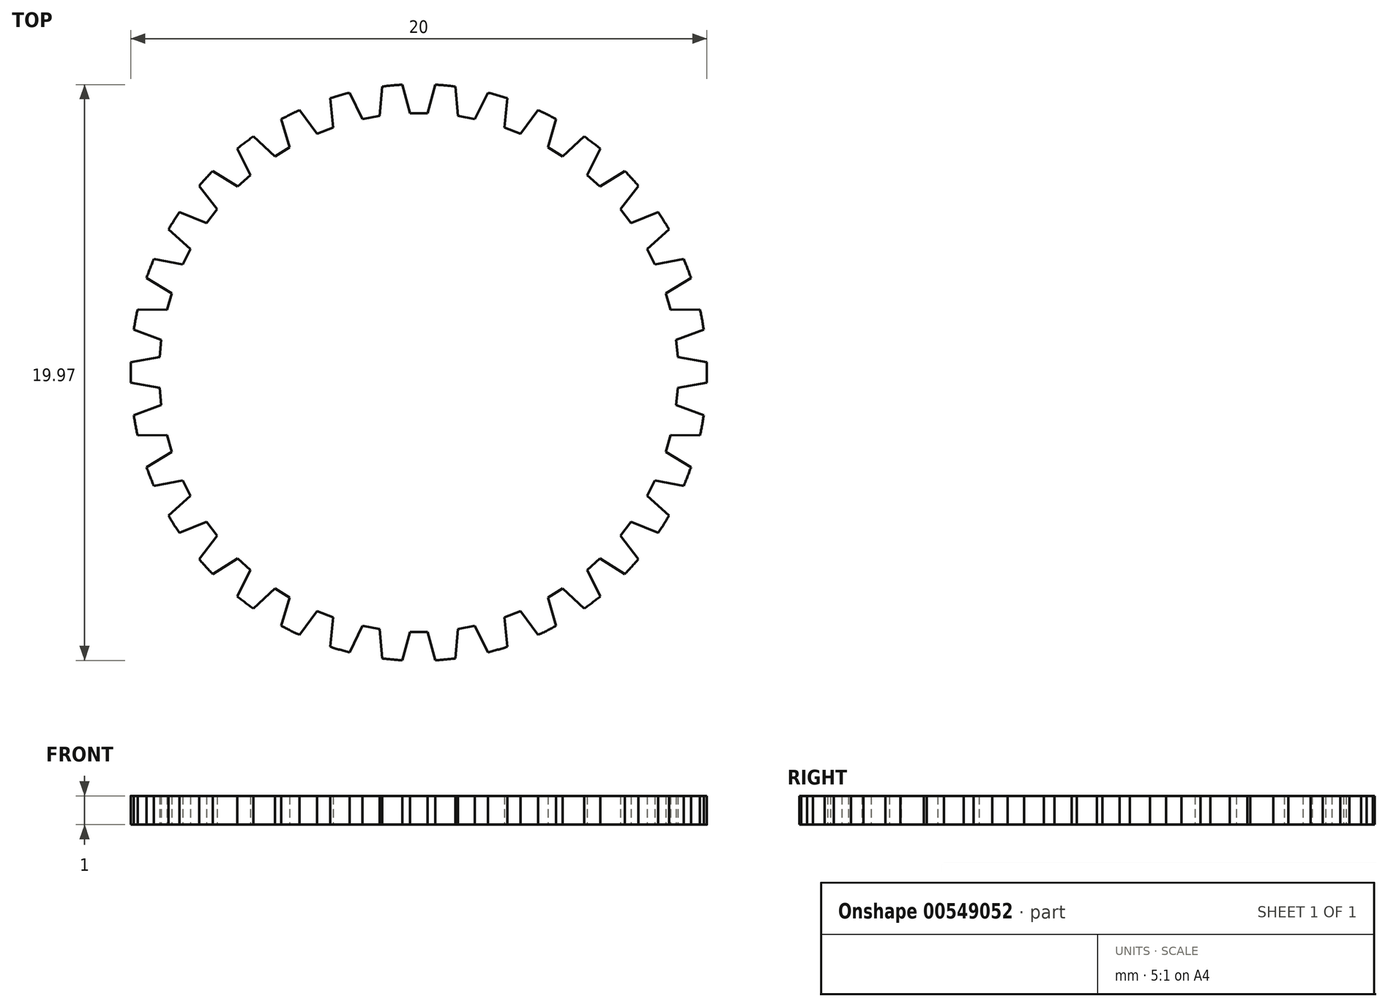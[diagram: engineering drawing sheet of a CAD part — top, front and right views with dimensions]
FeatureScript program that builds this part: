
annotation { "Feature Type Name" : "Feature", "Feature Type Description" : "" }
export const myFeature = defineFeature(function(context is Context, id is Id, definition is map)
    precondition{}
    {
        {
            var Q0;
            Q0=qCreatedBy(makeId("Top.planeOp"),FACE);
            var sketch = newSketch(context, id + "F0", { "sketchPlane" : qUnion([Q0])});
            skCircle(sketch, "E0", {"center": v(-41.3, 19.5) * mm, "radius": 10 * mm});
            skLineSegment(sketch, "E1", {"start": v(-41.3, 19.5) * mm, "end": v(-41.3, 32.24) * mm, "construction": true});
            skLineSegment(sketch, "E2", {"start": v(-41.86, 29.5) * mm, "end": v(-41.6, 28.5) * mm});
            skLineSegment(sketch, "E3", {"start": v(-41.6, 28.5) * mm, "end": v(-41.3, 28.5) * mm});
            skLineSegment(sketch, "E4.MirrorCS", {"start": v(-41, 28.5) * mm, "end": v(-41.3, 28.5) * mm});
            skLineSegment(sketch, "E5.MirrorCS", {"start": v(-40.72, 29.5) * mm, "end": v(-41, 28.5) * mm});
            skLineSegment(sketch, "E6.1.0", {"start": v(-42.56, 29.43) * mm, "end": v(-42.65, 28.4) * mm});
            skLineSegment(sketch, "E6.1.1", {"start": v(-42.65, 28.4) * mm, "end": v(-42.94, 28.35) * mm});
            skLineSegment(sketch, "E6.1.2", {"start": v(-43.24, 28.3) * mm, "end": v(-42.94, 28.35) * mm});
            skLineSegment(sketch, "E6.1.3", {"start": v(-43.69, 29.22) * mm, "end": v(-43.24, 28.3) * mm});
            skLineSegment(sketch, "E6.2.0", {"start": v(-44.36, 29.02) * mm, "end": v(-44.26, 28) * mm});
            skLineSegment(sketch, "E6.2.1", {"start": v(-44.26, 28) * mm, "end": v(-44.54, 27.9) * mm});
            skLineSegment(sketch, "E6.2.2", {"start": v(-44.82, 27.8) * mm, "end": v(-44.54, 27.9) * mm});
            skLineSegment(sketch, "E6.2.3", {"start": v(-45.43, 28.61) * mm, "end": v(-44.82, 27.8) * mm});
            skLineSegment(sketch, "E6.3.0", {"start": v(-46.06, 28.3) * mm, "end": v(-45.77, 27.32) * mm});
            skLineSegment(sketch, "E6.3.1", {"start": v(-45.77, 27.32) * mm, "end": v(-46.03, 27.16) * mm});
            skLineSegment(sketch, "E6.3.2", {"start": v(-46.28, 27) * mm, "end": v(-46.03, 27.16) * mm});
            skLineSegment(sketch, "E6.3.3", {"start": v(-47.03, 27.7) * mm, "end": v(-46.28, 27) * mm});
            skLineSegment(sketch, "E6.4.0", {"start": v(-47.6, 27.27) * mm, "end": v(-47.13, 26.36) * mm});
            skLineSegment(sketch, "E6.4.1", {"start": v(-47.13, 26.36) * mm, "end": v(-47.35, 26.16) * mm});
            skLineSegment(sketch, "E6.4.2", {"start": v(-47.58, 25.96) * mm, "end": v(-47.35, 26.16) * mm});
            skLineSegment(sketch, "E6.4.3", {"start": v(-48.44, 26.5) * mm, "end": v(-47.58, 25.96) * mm});
            skLineSegment(sketch, "E6.5.0", {"start": v(-48.91, 25.98) * mm, "end": v(-48.3, 25.17) * mm});
            skLineSegment(sketch, "E6.5.1", {"start": v(-48.3, 25.17) * mm, "end": v(-48.47, 24.93) * mm});
            skLineSegment(sketch, "E6.5.2", {"start": v(-48.65, 24.7) * mm, "end": v(-48.47, 24.93) * mm});
            skLineSegment(sketch, "E6.5.3", {"start": v(-49.6, 25.07) * mm, "end": v(-48.65, 24.7) * mm});
            skLineSegment(sketch, "E6.6.0", {"start": v(-49.97, 24.47) * mm, "end": v(-49.21, 23.79) * mm});
            skLineSegment(sketch, "E6.6.1", {"start": v(-49.21, 23.79) * mm, "end": v(-49.35, 23.52) * mm});
            skLineSegment(sketch, "E6.6.2", {"start": v(-49.48, 23.25) * mm, "end": v(-49.35, 23.52) * mm});
            skLineSegment(sketch, "E6.6.3", {"start": v(-50.48, 23.45) * mm, "end": v(-49.48, 23.25) * mm});
            skLineSegment(sketch, "E6.7.0", {"start": v(-50.74, 22.79) * mm, "end": v(-49.87, 22.26) * mm});
            skLineSegment(sketch, "E6.7.1", {"start": v(-49.87, 22.26) * mm, "end": v(-49.95, 21.97) * mm});
            skLineSegment(sketch, "E6.7.2", {"start": v(-50.03, 21.68) * mm, "end": v(-49.95, 21.97) * mm});
            skLineSegment(sketch, "E6.7.3", {"start": v(-51.05, 21.69) * mm, "end": v(-50.03, 21.68) * mm});
            skLineSegment(sketch, "E6.8.0", {"start": v(-51.18, 21) * mm, "end": v(-50.22, 20.64) * mm});
            skLineSegment(sketch, "E6.8.1", {"start": v(-50.22, 20.64) * mm, "end": v(-50.25, 20.34) * mm});
            skLineSegment(sketch, "E6.8.2", {"start": v(-50.28, 20.04) * mm, "end": v(-50.25, 20.34) * mm});
            skLineSegment(sketch, "E6.8.3", {"start": v(-51.28, 19.86) * mm, "end": v(-50.28, 20.04) * mm});
            skLineSegment(sketch, "E6.9.0", {"start": v(-51.28, 19.15) * mm, "end": v(-50.28, 18.98) * mm});
            skLineSegment(sketch, "E6.9.1", {"start": v(-50.28, 18.98) * mm, "end": v(-50.25, 18.68) * mm});
            skLineSegment(sketch, "E6.9.2", {"start": v(-50.22, 18.38) * mm, "end": v(-50.25, 18.68) * mm});
            skLineSegment(sketch, "E6.9.3", {"start": v(-51.18, 18.02) * mm, "end": v(-50.22, 18.38) * mm});
            skLineSegment(sketch, "E6.10.0", {"start": v(-51.05, 17.32) * mm, "end": v(-50.03, 17.33) * mm});
            skLineSegment(sketch, "E6.10.1", {"start": v(-50.03, 17.33) * mm, "end": v(-49.95, 17.04) * mm});
            skLineSegment(sketch, "E6.10.2", {"start": v(-49.87, 16.76) * mm, "end": v(-49.95, 17.04) * mm});
            skLineSegment(sketch, "E6.10.3", {"start": v(-50.74, 16.23) * mm, "end": v(-49.87, 16.76) * mm});
            skLineSegment(sketch, "E6.11.0", {"start": v(-50.48, 15.57) * mm, "end": v(-49.48, 15.76) * mm});
            skLineSegment(sketch, "E6.11.1", {"start": v(-49.48, 15.76) * mm, "end": v(-49.35, 15.5) * mm});
            skLineSegment(sketch, "E6.11.2", {"start": v(-49.21, 15.23) * mm, "end": v(-49.35, 15.5) * mm});
            skLineSegment(sketch, "E6.11.3", {"start": v(-49.97, 14.55) * mm, "end": v(-49.21, 15.23) * mm});
            skLineSegment(sketch, "E6.12.0", {"start": v(-49.6, 13.95) * mm, "end": v(-48.65, 14.32) * mm});
            skLineSegment(sketch, "E6.12.1", {"start": v(-48.65, 14.32) * mm, "end": v(-48.47, 14.08) * mm});
            skLineSegment(sketch, "E6.12.2", {"start": v(-48.3, 13.84) * mm, "end": v(-48.47, 14.08) * mm});
            skLineSegment(sketch, "E6.12.3", {"start": v(-48.91, 13.03) * mm, "end": v(-48.3, 13.84) * mm});
            skLineSegment(sketch, "E6.13.0", {"start": v(-48.44, 12.51) * mm, "end": v(-47.58, 13.06) * mm});
            skLineSegment(sketch, "E6.13.1", {"start": v(-47.58, 13.06) * mm, "end": v(-47.35, 12.86) * mm});
            skLineSegment(sketch, "E6.13.2", {"start": v(-47.13, 12.65) * mm, "end": v(-47.35, 12.86) * mm});
            skLineSegment(sketch, "E6.13.3", {"start": v(-47.6, 11.74) * mm, "end": v(-47.13, 12.65) * mm});
            skLineSegment(sketch, "E6.14.0", {"start": v(-47.03, 11.32) * mm, "end": v(-46.28, 12.01) * mm});
            skLineSegment(sketch, "E6.14.1", {"start": v(-46.28, 12.01) * mm, "end": v(-46.03, 11.86) * mm});
            skLineSegment(sketch, "E6.14.2", {"start": v(-45.77, 11.7) * mm, "end": v(-46.03, 11.86) * mm});
            skLineSegment(sketch, "E6.14.3", {"start": v(-46.06, 10.72) * mm, "end": v(-45.77, 11.7) * mm});
            skLineSegment(sketch, "E6.15.0", {"start": v(-45.43, 10.4) * mm, "end": v(-44.82, 11.22) * mm});
            skLineSegment(sketch, "E6.15.1", {"start": v(-44.82, 11.22) * mm, "end": v(-44.54, 11.12) * mm});
            skLineSegment(sketch, "E6.15.2", {"start": v(-44.26, 11) * mm, "end": v(-44.54, 11.12) * mm});
            skLineSegment(sketch, "E6.15.3", {"start": v(-44.36, 10) * mm, "end": v(-44.26, 11) * mm});
            skLineSegment(sketch, "E6.16.0", {"start": v(-43.69, 9.8) * mm, "end": v(-43.24, 10.72) * mm});
            skLineSegment(sketch, "E6.16.1", {"start": v(-43.24, 10.72) * mm, "end": v(-42.94, 10.66) * mm});
            skLineSegment(sketch, "E6.16.2", {"start": v(-42.65, 10.6) * mm, "end": v(-42.94, 10.66) * mm});
            skLineSegment(sketch, "E6.16.3", {"start": v(-42.56, 9.59) * mm, "end": v(-42.65, 10.6) * mm});
            skLineSegment(sketch, "E6.17.0", {"start": v(-41.86, 9.52) * mm, "end": v(-41.6, 10.5) * mm});
            skLineSegment(sketch, "E6.17.1", {"start": v(-41.6, 10.5) * mm, "end": v(-41.3, 10.5) * mm});
            skLineSegment(sketch, "E6.17.2", {"start": v(-41, 10.5) * mm, "end": v(-41.3, 10.5) * mm});
            skLineSegment(sketch, "E6.17.3", {"start": v(-40.72, 9.52) * mm, "end": v(-41, 10.5) * mm});
            skLineSegment(sketch, "E6.18.0", {"start": v(-40.02, 9.59) * mm, "end": v(-39.93, 10.6) * mm});
            skLineSegment(sketch, "E6.18.1", {"start": v(-39.93, 10.6) * mm, "end": v(-39.64, 10.66) * mm});
            skLineSegment(sketch, "E6.18.2", {"start": v(-39.34, 10.72) * mm, "end": v(-39.64, 10.66) * mm});
            skLineSegment(sketch, "E6.18.3", {"start": v(-38.9, 9.8) * mm, "end": v(-39.34, 10.72) * mm});
            skLineSegment(sketch, "E6.19.0", {"start": v(-38.22, 10) * mm, "end": v(-38.32, 11) * mm});
            skLineSegment(sketch, "E6.19.1", {"start": v(-38.32, 11) * mm, "end": v(-38.04, 11.12) * mm});
            skLineSegment(sketch, "E6.19.2", {"start": v(-37.76, 11.22) * mm, "end": v(-38.04, 11.12) * mm});
            skLineSegment(sketch, "E6.19.3", {"start": v(-37.15, 10.4) * mm, "end": v(-37.76, 11.22) * mm});
            skLineSegment(sketch, "E6.20.0", {"start": v(-36.52, 10.72) * mm, "end": v(-36.8, 11.7) * mm});
            skLineSegment(sketch, "E6.20.1", {"start": v(-36.8, 11.7) * mm, "end": v(-36.55, 11.86) * mm});
            skLineSegment(sketch, "E6.20.2", {"start": v(-36.3, 12.01) * mm, "end": v(-36.55, 11.86) * mm});
            skLineSegment(sketch, "E6.20.3", {"start": v(-35.55, 11.32) * mm, "end": v(-36.3, 12.01) * mm});
            skLineSegment(sketch, "E6.21.0", {"start": v(-34.99, 11.74) * mm, "end": v(-35.45, 12.65) * mm});
            skLineSegment(sketch, "E6.21.1", {"start": v(-35.45, 12.65) * mm, "end": v(-35.23, 12.86) * mm});
            skLineSegment(sketch, "E6.21.2", {"start": v(-35, 13.06) * mm, "end": v(-35.23, 12.86) * mm});
            skLineSegment(sketch, "E6.21.3", {"start": v(-34.14, 12.51) * mm, "end": v(-35, 13.06) * mm});
            skLineSegment(sketch, "E6.22.0", {"start": v(-33.67, 13.03) * mm, "end": v(-34.3, 13.84) * mm});
            skLineSegment(sketch, "E6.22.1", {"start": v(-34.3, 13.84) * mm, "end": v(-34.1, 14.08) * mm});
            skLineSegment(sketch, "E6.22.2", {"start": v(-33.93, 14.32) * mm, "end": v(-34.1, 14.08) * mm});
            skLineSegment(sketch, "E6.22.3", {"start": v(-32.98, 13.95) * mm, "end": v(-33.93, 14.32) * mm});
            skLineSegment(sketch, "E6.23.0", {"start": v(-32.6, 14.55) * mm, "end": v(-33.37, 15.23) * mm});
            skLineSegment(sketch, "E6.23.1", {"start": v(-33.37, 15.23) * mm, "end": v(-33.23, 15.5) * mm});
            skLineSegment(sketch, "E6.23.2", {"start": v(-33.1, 15.76) * mm, "end": v(-33.23, 15.5) * mm});
            skLineSegment(sketch, "E6.23.3", {"start": v(-32.1, 15.57) * mm, "end": v(-33.1, 15.76) * mm});
            skLineSegment(sketch, "E6.24.0", {"start": v(-31.84, 16.23) * mm, "end": v(-32.72, 16.76) * mm});
            skLineSegment(sketch, "E6.24.1", {"start": v(-32.72, 16.76) * mm, "end": v(-32.64, 17.04) * mm});
            skLineSegment(sketch, "E6.24.2", {"start": v(-32.55, 17.33) * mm, "end": v(-32.64, 17.04) * mm});
            skLineSegment(sketch, "E6.24.3", {"start": v(-31.53, 17.32) * mm, "end": v(-32.55, 17.33) * mm});
            skLineSegment(sketch, "E6.25.0", {"start": v(-31.4, 18.02) * mm, "end": v(-32.36, 18.38) * mm});
            skLineSegment(sketch, "E6.25.1", {"start": v(-32.36, 18.38) * mm, "end": v(-32.33, 18.68) * mm});
            skLineSegment(sketch, "E6.25.2", {"start": v(-32.3, 18.98) * mm, "end": v(-32.33, 18.68) * mm});
            skLineSegment(sketch, "E6.25.3", {"start": v(-31.3, 19.15) * mm, "end": v(-32.3, 18.98) * mm});
            skLineSegment(sketch, "E6.26.0", {"start": v(-31.3, 19.86) * mm, "end": v(-32.3, 20.04) * mm});
            skLineSegment(sketch, "E6.26.1", {"start": v(-32.3, 20.04) * mm, "end": v(-32.33, 20.34) * mm});
            skLineSegment(sketch, "E6.26.2", {"start": v(-32.36, 20.64) * mm, "end": v(-32.33, 20.34) * mm});
            skLineSegment(sketch, "E6.26.3", {"start": v(-31.4, 21) * mm, "end": v(-32.36, 20.64) * mm});
            skLineSegment(sketch, "E6.27.0", {"start": v(-31.53, 21.69) * mm, "end": v(-32.55, 21.68) * mm});
            skLineSegment(sketch, "E6.27.1", {"start": v(-32.55, 21.68) * mm, "end": v(-32.64, 21.97) * mm});
            skLineSegment(sketch, "E6.27.2", {"start": v(-32.72, 22.26) * mm, "end": v(-32.64, 21.97) * mm});
            skLineSegment(sketch, "E6.27.3", {"start": v(-31.84, 22.79) * mm, "end": v(-32.72, 22.26) * mm});
            skLineSegment(sketch, "E6.28.0", {"start": v(-32.1, 23.45) * mm, "end": v(-33.1, 23.25) * mm});
            skLineSegment(sketch, "E6.28.1", {"start": v(-33.1, 23.25) * mm, "end": v(-33.23, 23.52) * mm});
            skLineSegment(sketch, "E6.28.2", {"start": v(-33.37, 23.79) * mm, "end": v(-33.23, 23.52) * mm});
            skLineSegment(sketch, "E6.28.3", {"start": v(-32.6, 24.47) * mm, "end": v(-33.37, 23.79) * mm});
            skLineSegment(sketch, "E6.29.0", {"start": v(-32.98, 25.07) * mm, "end": v(-33.93, 24.7) * mm});
            skLineSegment(sketch, "E6.29.1", {"start": v(-33.93, 24.7) * mm, "end": v(-34.1, 24.93) * mm});
            skLineSegment(sketch, "E6.29.2", {"start": v(-34.3, 25.17) * mm, "end": v(-34.1, 24.93) * mm});
            skLineSegment(sketch, "E6.29.3", {"start": v(-33.67, 25.98) * mm, "end": v(-34.3, 25.17) * mm});
            skLineSegment(sketch, "E6.30.0", {"start": v(-34.14, 26.5) * mm, "end": v(-35, 25.96) * mm});
            skLineSegment(sketch, "E6.30.1", {"start": v(-35, 25.96) * mm, "end": v(-35.23, 26.16) * mm});
            skLineSegment(sketch, "E6.30.2", {"start": v(-35.45, 26.36) * mm, "end": v(-35.23, 26.16) * mm});
            skLineSegment(sketch, "E6.30.3", {"start": v(-34.99, 27.27) * mm, "end": v(-35.45, 26.36) * mm});
            skLineSegment(sketch, "E6.31.0", {"start": v(-35.55, 27.7) * mm, "end": v(-36.3, 27) * mm});
            skLineSegment(sketch, "E6.31.1", {"start": v(-36.3, 27) * mm, "end": v(-36.55, 27.16) * mm});
            skLineSegment(sketch, "E6.31.2", {"start": v(-36.8, 27.32) * mm, "end": v(-36.55, 27.16) * mm});
            skLineSegment(sketch, "E6.31.3", {"start": v(-36.52, 28.3) * mm, "end": v(-36.8, 27.32) * mm});
            skLineSegment(sketch, "E7.3.32.0", {"start": v(-37.76, 27.8) * mm, "end": v(-38.04, 27.9) * mm});
            skLineSegment(sketch, "E7.5.32.0", {"start": v(-37.15, 28.61) * mm, "end": v(-37.76, 27.8) * mm});
            skLineSegment(sketch, "E7.6.32.0", {"start": v(-38.32, 28) * mm, "end": v(-38.04, 27.9) * mm});
            skLineSegment(sketch, "E7.9.32.0", {"start": v(-38.22, 29.02) * mm, "end": v(-38.32, 28) * mm});
            skLineSegment(sketch, "E7.3.33.0", {"start": v(-39.34, 28.3) * mm, "end": v(-39.64, 28.35) * mm});
            skLineSegment(sketch, "E7.5.33.0", {"start": v(-38.9, 29.22) * mm, "end": v(-39.34, 28.3) * mm});
            skLineSegment(sketch, "E7.6.33.0", {"start": v(-39.93, 28.4) * mm, "end": v(-39.64, 28.35) * mm});
            skLineSegment(sketch, "E7.9.33.0", {"start": v(-40.02, 29.43) * mm, "end": v(-39.93, 28.4) * mm});
            skSolve(sketch);
        }
        {
            var Q0;
            {var subQ29=sQuery(id+"F0.wireOp",EDGE,"E2");Q0=makeQuery(id+"F0.imprint","IMPRINT",FACE,{"disambiguationData":[TD([[makeQuery(id+"F0.imprint","IMPRINT",EDGE,{"derivedFrom":subQ29}),-1.0]])]});}
            extrude(context, id + "F1", {"entities" : qUnion([Q0]), "depth" : 1 * mm, "offsetDistance" : 25 * mm});
        }
    });
